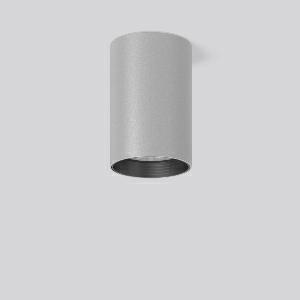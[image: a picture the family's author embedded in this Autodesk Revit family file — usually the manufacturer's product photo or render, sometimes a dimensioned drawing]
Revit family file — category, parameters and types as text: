
# Revit family: heledon_maxi_a_931220_004_3_fdb4
name_source: partatom
category: Lighting Fixtures
units: mm (PartAtom-declared; Revit-internal decimal feet)

## family parameters
Cut with Voids When Loaded = No
Host = Face
Light Source = No
Part Type = Normal
Room Calculation Point = No
Round Connector Dimension = Use Diameter
Shared = No

## types (1)
- HELEDON maxi A (1 x LED Modul 935, 2900 lm, 3500)
    Apparent Load = 25 VA
    Approval mark = CE
    CIE Flux Codes = 97 100 100 100 100
    Color Rendering = 92
    Color Temperature = 3500
    Default Elevation = 1800 mm
    Description = Series: HELEDON maxi
Cylindrical surface-mounted downlight. Housing: die-cast aluminium, powder-coated. Internal ceiling frame polycarbonate with bayonet mounting. Black plastic ring and recessed LED to prevent glare from the side. Optical assembly with lens made of plastic (polycarbonate) for the best homogeneous light distribution - can be changed without tools. Best colour rendering index Ra>90. Suitable for Ceiling mounting. Easy installation with a separate ceiling frame with bayonet mounting and plug connection. Driver integrated. Connected via plug-in connector. High quality converter without flickering and stroboscopic effect. The following accessories can be mounted without use of tools: interchangeable lenses, decorative glasses, honeycomb louvre, clear and frosted diffusers, white interchangeable plastic ring. 
Colour: silver
Diameter: 123 mm
Height: 183 mm
Lamp: LED
Socket: without socket
Colour temperature: 3500K
Colour rendering index (CRI): 92
System power: 25 W
Rated luminous flux: 2900 lm
Luminous efficiency: 116 lm/W
Control gear: Regulated power supply
Protection class: I
Type of protection: IP 20
    Height = 183 mm
    Lamp = 1 x LED Modul 935
    Lamp Light Flux = 2900 lm
    Lamp count = 1
    Length = 123 mm
    Lifetime = 50000 h
    Luminous efficacy = 116 lm/W
    Manufacturer = RZB
    ModVariant = No
    Model = 931220.004.3
    Mounting Place = Ceiling
    Mounting Type = Surface mounted
    Number of Poles = 1
    OnlyDefault = Yes
    Power Factor = 1
    Product Name = HELEDON maxi A
    Product group = Surface mounted downlights
    ProductGroupID = 302
    Protection Class = Protection class I
    Protection Degree = IP 20
    RLX_Detail_Level = 1
    RLX_Emergency_Light_Flux = 0 lm
    RLX_Emergency_Type = 0
    RLX_Emergency_Type_DB = No
    RlxData = <blob elided: 98445 chars, md5=72162253>
    Socket = socket
    Standby Power = 0 W
    System Light Flux = 2900 lm
    System Power = 25 W
    Type Comments = Product without accessories
    Type Image = 931193.004.jpg
    URL = http://relux.com
    VarID = ---
    Voltage = 230 V
    Voltage Range = 220-240 V
    Weight = 0.00 kg
    Width = 0 mm  [stored 0 ft]

note: [stored X ft] marks values corroborated as IEEE doubles in the binary element streams (Revit-internal decimal feet)

## geometry (parser evidence)
native form markers: Blend x4, Sweep x9
no freeform markers — native parametric forms only
